# Revit family: Layout-Teknion-Kiosk_03-R2020
name_source: partatom
category: Furniture Systems
units: mm (PartAtom-declared; Revit-internal decimal feet)

## family parameters
Always vertical = Yes
Cut with Voids When Loaded = No
OmniClass Number = 23.40.70.14.64.21
OmniClass Title = Systems Furniture
Part Type = Normal
Room Calculation Point = No
Round Connector Dimension = Use Diameter
Shared = Yes
Work Plane-Based = No

## types (1)
- Kiosk 03
    Assembly Code = E2020200
    Default Elevation = 0 "
    Description = 16'-9 1/2" x 11'-4 1/2" Overall
    Manufacturer = Teknion
    Manufacturer Fax = 416.661.4586
    Model = Kiosk Layout 03
    Product Line = Kiosk
    Product Page URL = https://www.teknionplanningtool.com
    Series = Kiosk
    Sustainability Data = https://www.teknion.com
    URL = www.teknion.com
    Unit Weight URL = http://www.teknion.com
    Warranty = http://www.teknion.com

## geometry (parser evidence)
native form markers: Blend x14, Sweep x27
no freeform markers — native parametric forms only
